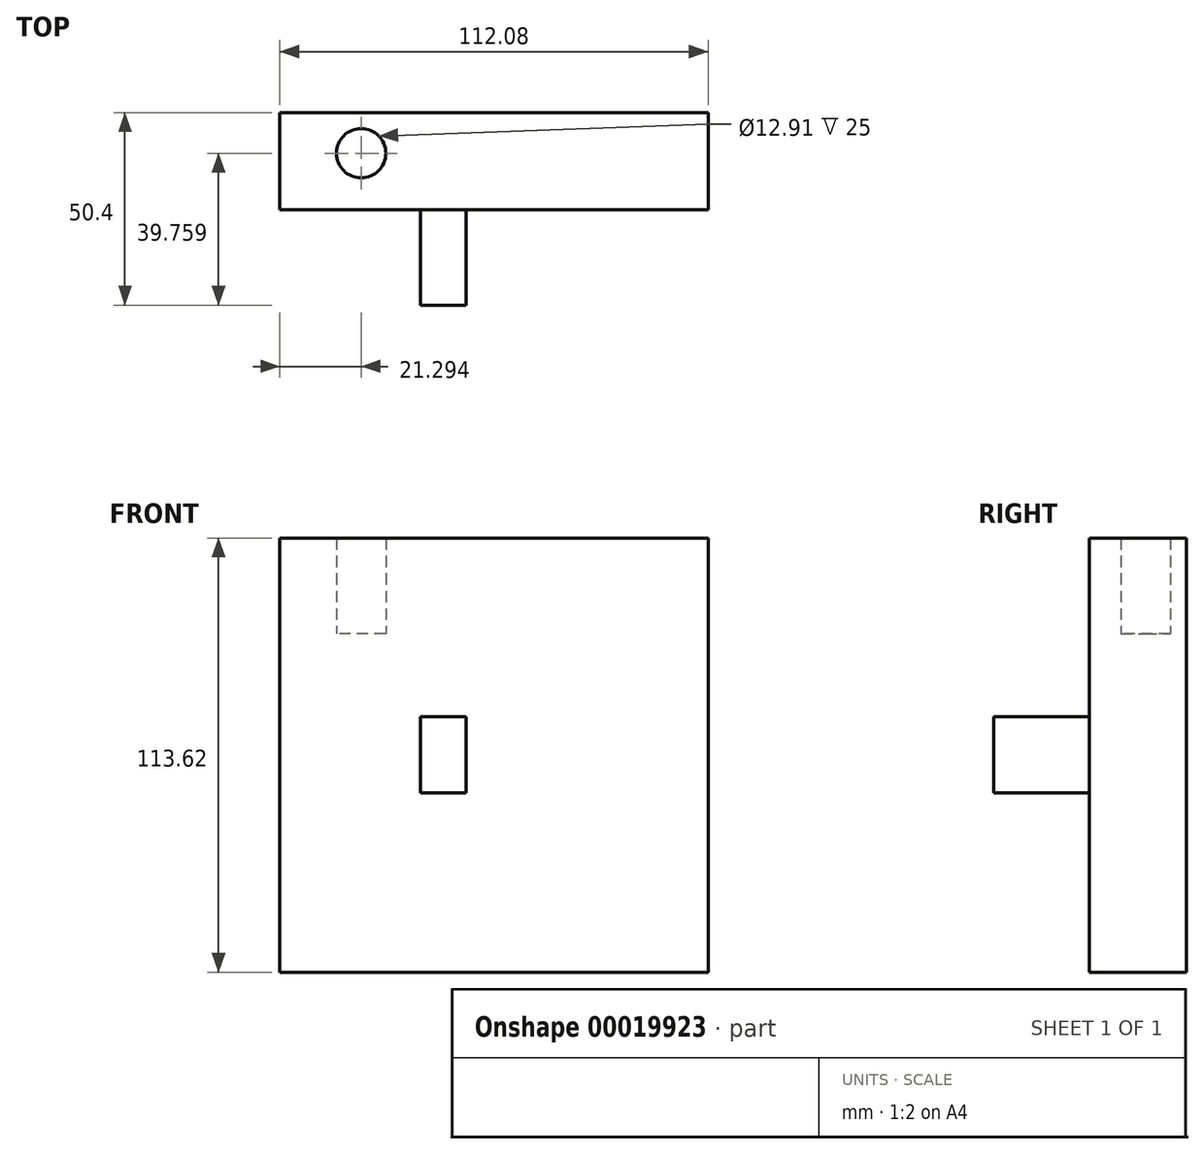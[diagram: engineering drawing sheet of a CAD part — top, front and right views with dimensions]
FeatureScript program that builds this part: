
annotation { "Feature Type Name" : "Feature", "Feature Type Description" : "" }
export const myFeature = defineFeature(function(context is Context, id is Id, definition is map)
    precondition{}
    {
        {
            var Q0;
            Q0=qCreatedBy(makeId("Front.planeOp"),FACE);
            var sketch = newSketch(context, id + "F0", { "sketchPlane" : qUnion([Q0])});
            skLineSegment(sketch, "E0.bottom", {"start": v(-55.7, 41.7) * mm, "end": v(56.38, 41.7) * mm});
            skLineSegment(sketch, "E0.top", {"start": v(-55.7, -46.93) * mm, "end": v(56.38, -46.93) * mm});
            skLineSegment(sketch, "E0.left", {"start": v(-55.7, 41.7) * mm, "end": v(-55.7, -46.93) * mm});
            skLineSegment(sketch, "E0.right", {"start": v(56.38, 41.7) * mm, "end": v(56.38, -46.93) * mm});
            skSolve(sketch);
        }
        {
            var Q0;
            Q0=makeQuery(id+"F0.imprint","IMPRINT",FACE,{"disambiguationData":[TD([[makeQuery(id+"F0.imprint","IMPRINT",EDGE,{"derivedFrom":sQuery(id+"F0.wireOp",EDGE,"E0.bottom")}),-1.0]])]});
            extrude(context, id + "F1", {"entities" : qUnion([Q0]), "depth" : 25.4 * mm});
        }
        {
            var Q0;
            Q0=qCreatedBy(makeId("Front.planeOp"),FACE);
            var sketch = newSketch(context, id + "F2", { "sketchPlane" : qUnion([Q0])});
            skCircle(sketch, "E1", {"center": v(24.55, 0) * mm, "radius": 10 * mm});
            skSolve(sketch);
        }
        {
            var Q0;
            Q0=sQuery(id+"F2.wireOp",EDGE,"E1");
            extrude(context, id + "F3", {"bodyType" : ToolBodyType.SURFACE, "surfaceEntities" : qUnion([Q0]), "depth" : 50 * mm, "hasSecondDirection" : true, "secondDirectionOppositeDirection" : true, "secondDirectionDepth" : 25.4 * mm});
        }
        {
            var Q0;
            Q0=makeQuery(id+"F1.opExtrude","SWEPT_FACE",FACE,{"disambiguationData":[OSD([sQuery(id+"F0.wireOp",EDGE,"E0.bottom")])]});
            var sketch = newSketch(context, id + "F4", { "sketchPlane" : qUnion([Q0])});
            skCircle(sketch, "E2", {"center": v(-34.4, -10.64) * mm, "radius": 6.45 * mm});
            skSolve(sketch);
        }
        {
            var Q0;
            Q0=makeQuery(id+"F4.imprint","IMPRINT",FACE,{"disambiguationData":[TD([[makeQuery(id+"F4.imprint","IMPRINT",EDGE,{"derivedFrom":sQuery(id+"F4.wireOp",EDGE,"E2")}),-1.0]])]});
            extrude(context, id + "F5", {"entities" : qUnion([Q0]), "operationType" : NewBodyOperationType.ADD, "depth" : 25 * mm});
        }
        {
            var Q0;
            {var subQ0=sQuery(id+"F0.wireOp",EDGE,"E0.bottom");Q0=makeQuery(id+"F5.boolean.opBoolean","MERGE",FACE,{"derivedFrom":[makeQuery(id+"F1.opExtrude","CAP_FACE",FACE,{"disambiguationData":[OSD([subQ0,sQuery(id+"F0.wireOp",EDGE,"E0.top"),sQuery(id+"F0.wireOp",EDGE,"E0.left"),sQuery(id+"F0.wireOp",EDGE,"E0.right")])],"isStart":false}),makeQuery(id+"F5.opExtrude","SWEPT_FACE",FACE,{"disambiguationData":[OSD([subQ0]),TDD([makeQuery(id+"F4.imprint","IMPRINT",EDGE,{"derivedFrom":makeQuery(id+"F1.opExtrude","CAP_EDGE",EDGE,{"disambiguationData":[OSD([subQ0])],"isStart":false})})])]})]});}
            var sketch = newSketch(context, id + "F6", { "sketchPlane" : qUnion([Q0])});
            skLineSegment(sketch, "E3.bottom", {"start": v(-18.85, 20) * mm, "end": v(-6.9, 20) * mm});
            skLineSegment(sketch, "E3.top", {"start": v(-18.85, 0) * mm, "end": v(-6.9, 0) * mm});
            skLineSegment(sketch, "E3.left", {"start": v(-18.85, 20) * mm, "end": v(-18.85, 0) * mm});
            skLineSegment(sketch, "E3.right", {"start": v(-6.9, 20) * mm, "end": v(-6.9, 0) * mm});
            skSolve(sketch);
        }
        {
            var Q0;
            Q0=makeQuery(id+"F6.imprint","IMPRINT",FACE,{"disambiguationData":[TD([[makeQuery(id+"F6.imprint","IMPRINT",EDGE,{"derivedFrom":sQuery(id+"F6.wireOp",EDGE,"E3.bottom")}),-1.0]])]});
            extrude(context, id + "F7", {"entities" : qUnion([Q0]), "operationType" : NewBodyOperationType.ADD, "depth" : 25 * mm});
        }
    });
